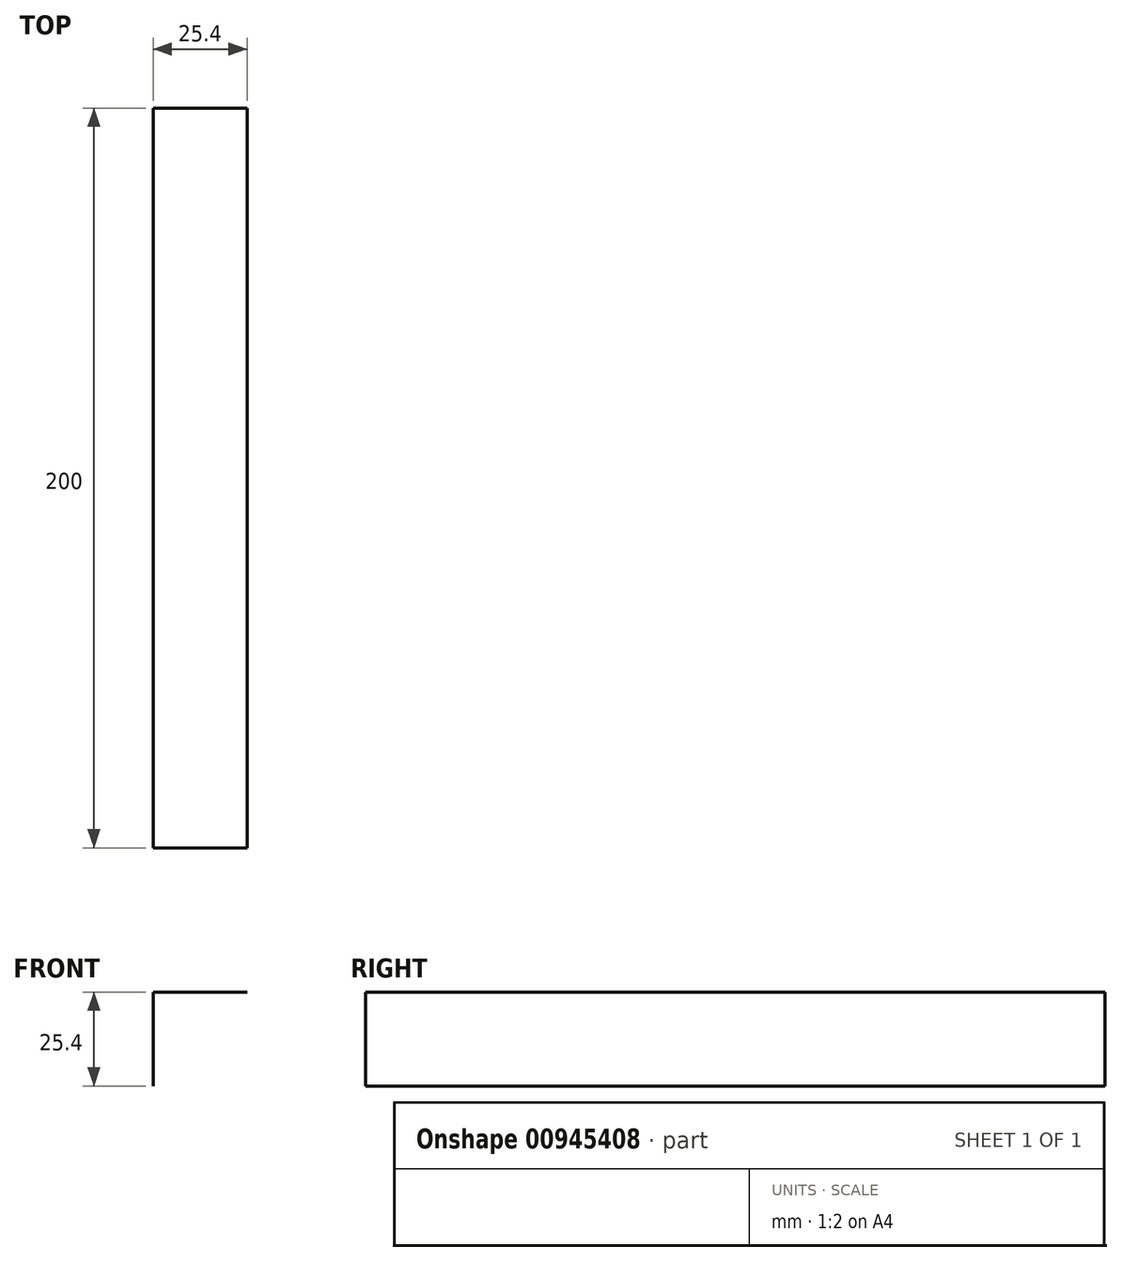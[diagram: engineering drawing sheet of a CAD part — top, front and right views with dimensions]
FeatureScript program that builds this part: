
annotation { "Feature Type Name" : "Feature", "Feature Type Description" : "" }
export const myFeature = defineFeature(function(context is Context, id is Id, definition is map)
    precondition{}
    {
        {
            var Q0;
            Q0=qCreatedBy(makeId("Front.planeOp"),FACE);
            var sketch = newSketch(context, id + "F0", { "sketchPlane" : qUnion([Q0])});
            skLineSegment(sketch, "E0.bottom", {"start": v(-15.33, -1.06) * mm, "end": v(10.07, -1.06) * mm});
            skLineSegment(sketch, "E0.left", {"start": v(-15.33, -1.06) * mm, "end": v(-15.33, -26.46) * mm});
            skSolve(sketch);
        }
        {
            var Q0;
            Q0=sQuery(id+"F0.wireOp",EDGE,"E0.bottom");
            var Q1;
            Q1=sQuery(id+"F0.wireOp",EDGE,"E0.left");
            extrude(context, id + "F1", {"bodyType" : ToolBodyType.SURFACE, "surfaceEntities" : qUnion([Q0, Q1]), "depth" : 200 * mm, "offsetDistance" : 25.4 * mm});
        }
    });
